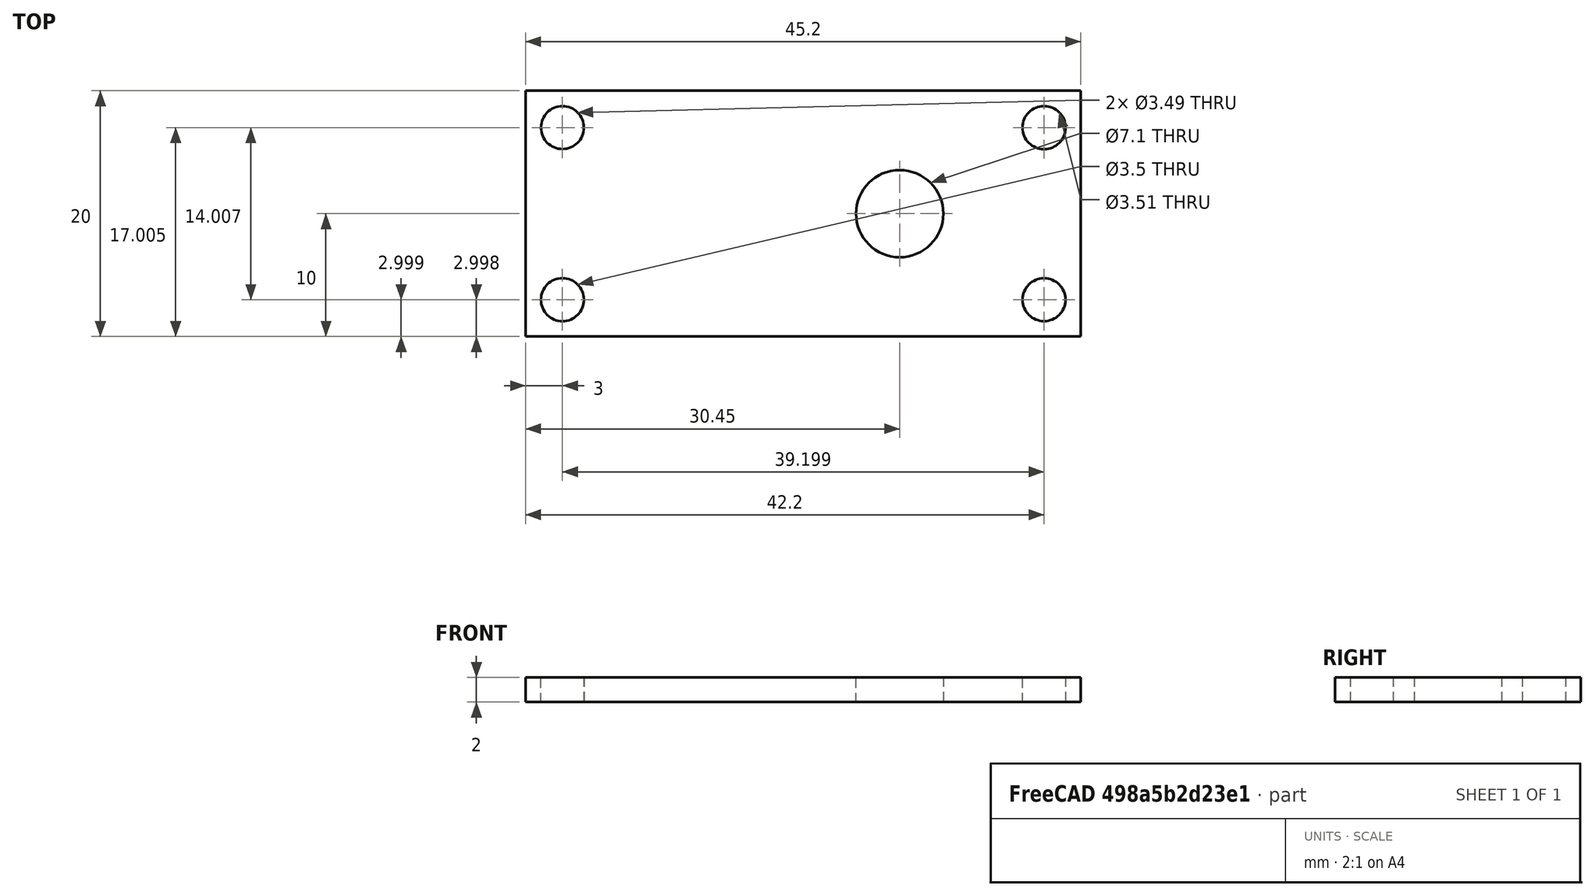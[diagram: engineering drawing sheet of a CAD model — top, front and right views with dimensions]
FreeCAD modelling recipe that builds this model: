
FCSTD DOCUMENT  (FreeCAD 0.17R13522 (Git))
Label: base_inferior_con_agujeros_v2
License: CreativeCommons Attribution-ShareAlike
LicenseURL: http://creativecommons.org/licenses/by-sa/4.0/
objects: Part::Part2DObjectPython×7, Part::Extrusion×5, Part::Cut×5, Part::Box×1, Part::Feature×1
note: 19 computed .brp shape members not serialized (recipe doc carries the construction recipe); baked Part::Feature solids carry a one-line shape summary decoded from their .brp

FEATURE [Part::Box] Box  label="placa base"
  AttacherType = Attacher::AttachEngine3D
  Height = 2
  Length = 45.2
  Width = 20
FEATURE [Part::Part2DObjectPython] Circle  label="taladro inferior izquierdo"  # Draft 2D object (typed FeaturePython)
  FirstAngle = 0
  LastAngle = 0
  MakeFace = false
  Placement = pos=(3,2.99873,2) rot=(0,0,1;3.14159rad)
  Radius = 1.74945
FEATURE [Part::Part2DObjectPython] Circle001  label="taladro inferior derecho"  # Draft 2D object (typed FeaturePython)
  FirstAngle = 0
  LastAngle = 0
  MakeFace = false
  Placement = pos=(42.1991,2.99781,2) rot=(0,0,1;3.14159rad)
  Radius = 1.7464
FEATURE [Part::Part2DObjectPython] Circle002  label="taladro superior derecho"  # Draft 2D object (typed FeaturePython)
  FirstAngle = 0
  LastAngle = 0
  MakeFace = false
  Placement = pos=(42.2,17.005,2) rot=(0,0,1;3.14159rad)
  Radius = 1.75369
FEATURE [Part::Part2DObjectPython] Circle003  label="taladro superior izquierdo"  # Draft 2D object (typed FeaturePython)
  FirstAngle = 0
  LastAngle = 0
  MakeFace = false
  Placement = pos=(3,17.005,2) rot=(0,0,1;3.14159rad)
  Radius = 1.74699
FEATURE [Part::Extrusion] Extrude
  Base = -> Circle003
  Dir = (0,0,1)
  DirMode = 2
  FaceMakerClass = Part::FaceMakerBullseye
  LengthFwd = 10
  LengthRev = 0
  Placement = pos=(0,0,-5) rot=(0,0,1;0rad)
  Solid = true
  Symmetric = false
FEATURE [Part::Extrusion] Extrude001
  Base = -> Circle
  Dir = (0,0,1)
  DirMode = 2
  FaceMakerClass = Part::FaceMakerBullseye
  LengthFwd = 10
  LengthRev = 0
  Placement = pos=(0,0,-5) rot=(0,0,1;0rad)
  Solid = true
  Symmetric = false
FEATURE [Part::Extrusion] Extrude002
  Base = -> Circle001
  Dir = (0,0,1)
  DirMode = 2
  FaceMakerClass = Part::FaceMakerBullseye
  LengthFwd = 10
  LengthRev = 0
  Placement = pos=(0,0,-5) rot=(0,0,1;0rad)
  Solid = true
  Symmetric = false
FEATURE [Part::Extrusion] Extrude003
  Base = -> Circle002
  Dir = (0,0,1)
  DirMode = 2
  FaceMakerClass = Part::FaceMakerBullseye
  LengthFwd = 10
  LengthRev = 0
  Placement = pos=(0,0,-5) rot=(0,0,1;0rad)
  Solid = true
  Symmetric = false
FEATURE [Part::Cut] Cut
  Base = -> Box
  Refine = true
  Tool = -> Extrude001
FEATURE [Part::Cut] Cut001
  Base = -> Cut
  Refine = true
  Tool = -> Extrude
FEATURE [Part::Cut] Cut002
  Base = -> Cut001
  Refine = true
  Tool = -> Extrude002
FEATURE [Part::Cut] Cut003  label="base con taladros en esquina"
  Base = -> Cut002
  Refine = true
  Tool = -> Extrude003
FEATURE [Part::Part2DObjectPython] Circle004  # Draft 2D object (typed FeaturePython)
  FirstAngle = 0
  LastAngle = 0
  MakeFace = false
  Placement = pos=(30.45,10,2) rot=(0,0,1;3.14159rad)
  Radius = 3.55
FEATURE [Part::Extrusion] Extrude004
  Base = -> Circle004
  Dir = (0,0,1)
  DirMode = 2
  FaceMakerClass = Part::FaceMakerBullseye
  LengthFwd = 10
  LengthRev = 0
  Placement = pos=(0,0,-4) rot=(0,0,1;0rad)
  Solid = true
  Symmetric = false
FEATURE [Part::Cut] Cut004  label="base con agujeros"
  Base = -> Cut003
  Refine = true
  Tool = -> Extrude004
FEATURE [Part::Part2DObjectPython] Rectangle  # Draft 2D object (typed FeaturePython)
  ChamferSize = 0
  Columns = 1
  FilletRadius = 0
  Height = 5
  Length = 5
  MakeFace = false
  Placement = pos=(23.95,12.5,2) rot=(0,0,1;3.14159rad)
  Rows = 1
FEATURE [Part::Part2DObjectPython] Rectangle001  # Draft 2D object (typed FeaturePython)
  ChamferSize = 0
  Columns = 1
  FilletRadius = 0
  Height = 5
  Length = -5
  MakeFace = false
  Placement = pos=(36.95,12.5,2) rot=(0,0,1;3.14159rad)
  Rows = 1
FEATURE [Part::Feature] Cut004_solid001001  label="base con agujeros (Solid)002"
  shape: bbox 45.2 x 20 x 2 mm, 11 faces (baked)
